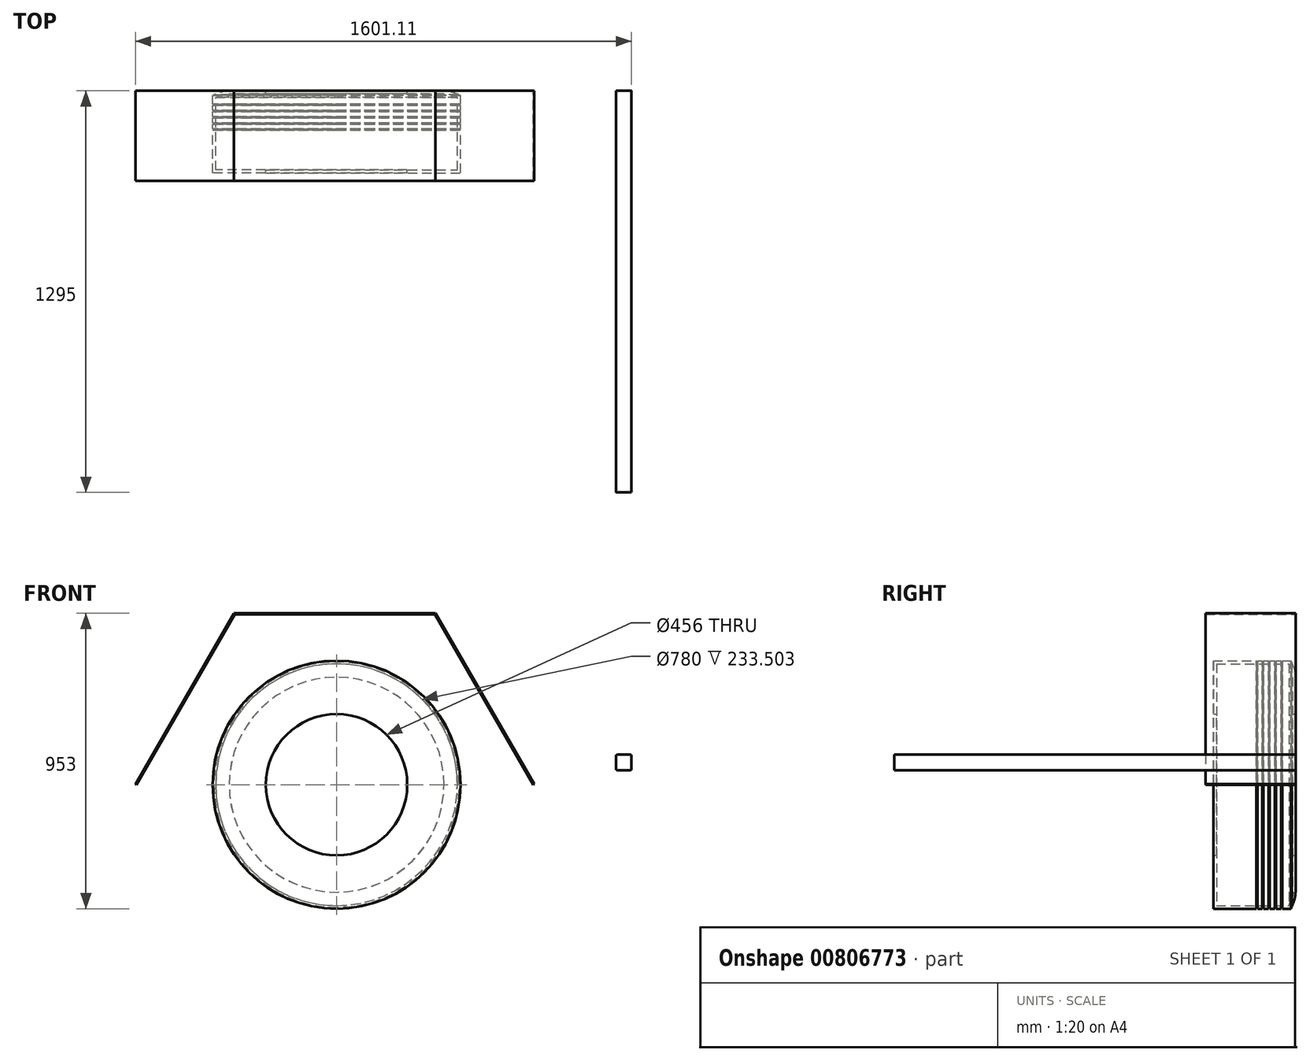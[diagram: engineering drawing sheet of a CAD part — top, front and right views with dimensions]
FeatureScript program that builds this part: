
annotation { "Feature Type Name" : "Feature", "Feature Type Description" : "" }
export const myFeature = defineFeature(function(context is Context, id is Id, definition is map)
    precondition{}
    {
        {
            var Q0;
            Q0=qCreatedBy(makeId("Front.planeOp"),FACE);
            var sketch = newSketch(context, id + "F0", { "sketchPlane" : qUnion([Q0])});
            skCircle(sketch, "E0", {"center": v(0, 0) * mm, "radius": 400 * mm});
            skCircle(sketch, "E1.0", {"center": v(0, 0) * mm, "radius": 228 * mm});
            skSolve(sketch);
        }
        {
            var Q0;
            Q0=makeQuery(id+"F0.imprint","IMPRINT",FACE,{"disambiguationData":[TD([[makeQuery(id+"F0.imprint","IMPRINT",EDGE,{"derivedFrom":sQuery(id+"F0.wireOp",EDGE,"E0")}),1.0]])]});
            extrude(context, id + "F1", {"entities" : qUnion([Q0]), "depth" : 265 * mm, "offsetDistance" : 25 * mm});
        }
        {
            var Q0;
            Q0=qCreatedBy(makeId("Right.planeOp"),FACE);
            var sketch = newSketch(context, id + "F2", { "sketchPlane" : qUnion([Q0])});
            skLineSegment(sketch, "E2", {"start": v(-265, 400) * mm, "end": v(0, 400) * mm});
            skLineSegment(sketch, "E3.0", {"start": v(-265, -400) * mm, "end": v(-265, 400) * mm});
            skLineSegment(sketch, "E4", {"start": v(0, 228) * mm, "end": v(-265, 228) * mm});
            skLineSegment(sketch, "E5", {"start": v(-15, 400) * mm, "end": v(-15, 228) * mm, "construction": true});
            skLineSegment(sketch, "E6", {"start": v(-25, 400) * mm, "end": v(-25, 228) * mm, "construction": true});
            skFitSpline(sketch, "E7", {"points": [v(-15, 400) * mm, v(0, 346.7) * mm, v(-25, 228) * mm], "startDerivative": vector(53.15, -118.74) * mm, "endDerivative": vector(-65.5, -218.8) * mm});
            skArc(sketch, "E8", {"start": v(-12.04, 393.34) * mm, "mid": v(-16.38, 398.48) * mm, "end": v(-22.93, 400) * mm});
            skPoint(sketch, "E8.first.point", {"position": v(-12.33, 393.99) * mm});
            skPoint(sketch, "E8.second.point", {"position": v(-16.14, 398.33) * mm});
            skPoint(sketch, "E8.third.point", {"position": v(-22.93, 400) * mm});
            skLineSegment(sketch, "E9", {"start": v(-132.5, 400) * mm, "end": v(-132.5, -399.15) * mm, "construction": true});
            skArc(sketch, "E10.MirrorCS", {"start": v(-252.96, 393.34) * mm, "mid": v(-248.62, 398.48) * mm, "end": v(-242.07, 400) * mm});
            skFitSpline(sketch, "E11.MirrorCS", {"points": [v(-250, 400) * mm, v(-265, 346.7) * mm, v(-240, 228) * mm], "startDerivative": vector(-53.15, -118.74) * mm, "endDerivative": vector(65.5, -218.8) * mm});
            skLineSegment(sketch, "E12", {"start": v(-22.93, 400) * mm, "end": v(0, 400) * mm});
            skLineSegment(sketch, "E13", {"start": v(0, 400) * mm, "end": v(0, 228) * mm});
            skLineSegment(sketch, "E14", {"start": v(0, 228) * mm, "end": v(-25, 228) * mm});
            skLineSegment(sketch, "E15", {"start": v(-242.07, 400) * mm, "end": v(-265, 400) * mm});
            skLineSegment(sketch, "E16", {"start": v(-265, 400) * mm, "end": v(-265, 228) * mm});
            skLineSegment(sketch, "E17", {"start": v(-265, 228) * mm, "end": v(-240, 228) * mm});
            skLineSegment(sketch, "E18.bottom", {"start": v(-138.22, 400) * mm, "end": v(-141.84, 400) * mm});
            skLineSegment(sketch, "E18.top", {"start": v(-138.22, 395.6) * mm, "end": v(-141.84, 395.6) * mm});
            skLineSegment(sketch, "E18.left", {"start": v(-138.22, 400) * mm, "end": v(-138.22, 395.6) * mm});
            skLineSegment(sketch, "E18.right", {"start": v(-141.84, 400) * mm, "end": v(-141.84, 395.6) * mm});
            skLineSegment(sketch, "E19.1.0.0", {"start": v(-158.22, 400) * mm, "end": v(-161.84, 400) * mm});
            skLineSegment(sketch, "E19.1.0.1", {"start": v(-158.22, 400) * mm, "end": v(-158.22, 395.6) * mm});
            skLineSegment(sketch, "E19.1.0.2", {"start": v(-161.84, 400) * mm, "end": v(-161.84, 395.6) * mm});
            skLineSegment(sketch, "E19.1.0.3", {"start": v(-158.22, 395.6) * mm, "end": v(-161.84, 395.6) * mm});
            skLineSegment(sketch, "E19.2.0.0", {"start": v(-178.22, 400) * mm, "end": v(-181.84, 400) * mm});
            skLineSegment(sketch, "E19.2.0.1", {"start": v(-178.22, 400) * mm, "end": v(-178.22, 395.6) * mm});
            skLineSegment(sketch, "E19.2.0.2", {"start": v(-181.84, 400) * mm, "end": v(-181.84, 395.6) * mm});
            skLineSegment(sketch, "E19.2.0.3", {"start": v(-178.22, 395.6) * mm, "end": v(-181.84, 395.6) * mm});
            skLineSegment(sketch, "E19.3.0.0", {"start": v(-198.22, 400) * mm, "end": v(-201.84, 400) * mm});
            skLineSegment(sketch, "E19.3.0.1", {"start": v(-198.22, 400) * mm, "end": v(-198.22, 395.6) * mm});
            skLineSegment(sketch, "E19.3.0.2", {"start": v(-201.84, 400) * mm, "end": v(-201.84, 395.6) * mm});
            skLineSegment(sketch, "E19.3.0.3", {"start": v(-198.22, 395.6) * mm, "end": v(-201.84, 395.6) * mm});
            skLineSegment(sketch, "E19.4.0.0", {"start": v(-218.22, 400) * mm, "end": v(-221.84, 400) * mm});
            skLineSegment(sketch, "E19.4.0.1", {"start": v(-218.22, 400) * mm, "end": v(-218.22, 395.6) * mm});
            skLineSegment(sketch, "E19.4.0.2", {"start": v(-221.84, 400) * mm, "end": v(-221.84, 395.6) * mm});
            skLineSegment(sketch, "E19.4.0.3", {"start": v(-218.22, 395.6) * mm, "end": v(-221.84, 395.6) * mm});
            skLineSegment(sketch, "E19.5.0.0", {"start": v(-238.22, 400) * mm, "end": v(-241.84, 400) * mm});
            skLineSegment(sketch, "E19.5.0.1", {"start": v(-238.22, 400) * mm, "end": v(-238.22, 395.6) * mm});
            skLineSegment(sketch, "E19.5.0.2", {"start": v(-241.84, 400) * mm, "end": v(-241.84, 395.6) * mm});
            skLineSegment(sketch, "E19.5.0.3", {"start": v(-238.22, 395.6) * mm, "end": v(-241.84, 395.6) * mm});
            skLineSegment(sketch, "E19.direction1", {"start": v(-141.84, 400) * mm, "end": v(-161.84, 400) * mm, "construction": true});
            skLineSegment(sketch, "E20.MirrorCS", {"start": v(-26.78, 400) * mm, "end": v(-23.16, 400) * mm});
            skLineSegment(sketch, "E21.MirrorCS", {"start": v(-23.16, 400) * mm, "end": v(-23.16, 395.6) * mm});
            skLineSegment(sketch, "E22.MirrorCS", {"start": v(-26.78, 395.6) * mm, "end": v(-23.16, 395.6) * mm});
            skLineSegment(sketch, "E23.MirrorCS", {"start": v(-26.78, 400) * mm, "end": v(-26.78, 395.6) * mm});
            skLineSegment(sketch, "E24.MirrorCS", {"start": v(-43.16, 400) * mm, "end": v(-43.16, 395.6) * mm});
            skLineSegment(sketch, "E25.MirrorCS", {"start": v(-46.78, 395.6) * mm, "end": v(-43.16, 395.6) * mm});
            skLineSegment(sketch, "E26.MirrorCS", {"start": v(-46.78, 400) * mm, "end": v(-46.78, 395.6) * mm});
            skLineSegment(sketch, "E27.MirrorCS", {"start": v(-46.78, 400) * mm, "end": v(-43.16, 400) * mm});
            skLineSegment(sketch, "E28.MirrorCS", {"start": v(-63.16, 400) * mm, "end": v(-63.16, 395.6) * mm});
            skLineSegment(sketch, "E29.MirrorCS", {"start": v(-66.78, 395.6) * mm, "end": v(-63.16, 395.6) * mm});
            skLineSegment(sketch, "E30.MirrorCS", {"start": v(-66.78, 400) * mm, "end": v(-66.78, 395.6) * mm});
            skLineSegment(sketch, "E31.MirrorCS", {"start": v(-66.78, 400) * mm, "end": v(-63.16, 400) * mm});
            skLineSegment(sketch, "E32.MirrorCS", {"start": v(-83.16, 400) * mm, "end": v(-83.16, 395.6) * mm});
            skLineSegment(sketch, "E33.MirrorCS", {"start": v(-86.78, 395.6) * mm, "end": v(-83.16, 395.6) * mm});
            skLineSegment(sketch, "E34.MirrorCS", {"start": v(-86.78, 400) * mm, "end": v(-86.78, 395.6) * mm});
            skLineSegment(sketch, "E35.MirrorCS", {"start": v(-86.78, 400) * mm, "end": v(-83.16, 400) * mm});
            skLineSegment(sketch, "E36.MirrorCS", {"start": v(-103.16, 400) * mm, "end": v(-103.16, 395.6) * mm});
            skLineSegment(sketch, "E37.MirrorCS", {"start": v(-106.78, 395.6) * mm, "end": v(-103.16, 395.6) * mm});
            skLineSegment(sketch, "E38.MirrorCS", {"start": v(-106.78, 400) * mm, "end": v(-106.78, 395.6) * mm});
            skLineSegment(sketch, "E39.MirrorCS", {"start": v(-106.78, 400) * mm, "end": v(-103.16, 400) * mm});
            skLineSegment(sketch, "E40.MirrorCS", {"start": v(-123.16, 400) * mm, "end": v(-123.16, 395.6) * mm});
            skLineSegment(sketch, "E41.MirrorCS", {"start": v(-126.78, 395.6) * mm, "end": v(-123.16, 395.6) * mm});
            skLineSegment(sketch, "E42.MirrorCS", {"start": v(-126.78, 400) * mm, "end": v(-126.78, 395.6) * mm});
            skLineSegment(sketch, "E43.MirrorCS", {"start": v(-126.78, 400) * mm, "end": v(-123.16, 400) * mm});
            skSolve(sketch);
        }
        {
            var Q0;
            Q0=qCreatedBy(makeId("Right.planeOp"),FACE);
            var sketch = newSketch(context, id + "F3", { "sketchPlane" : qUnion([Q0])});
            skLineSegment(sketch, "E44", {"start": v(0, 0) * mm, "end": v(-286.12, 0) * mm, "construction": true});
            skSolve(sketch);
        }
        {
            var Q0;
            {var subQ0=sQuery(id+"F2.wireOp",EDGE,"E17");Q0=makeQuery(id+"F2.imprint","IMPRINT",FACE,{"disambiguationData":[TD([[makeQuery(id+"F2.imprint","IMPRINT",EDGE,{"derivedFrom":subQ0}),1.0]])]});}
            var Q1;
            {var subQ3=sQuery(id+"F2.wireOp",EDGE,"E10.MirrorCS");var subQ5=sQuery(id+"F2.wireOp",EDGE,"E11.MirrorCS");var subQ6=makeQuery(id+"F2.imprint","INTERSECT",VERTEX,{"disambiguationData":[OD(0.0)],"derivedFrom":[subQ3,subQ5]});Q1=makeQuery(id+"F2.imprint","IMPRINT",FACE,{"disambiguationData":[TD([[makeQuery(id+"F2.imprint","IMPRINT",EDGE,{"disambiguationData":[TD([[subQ6,-1.0]])],"derivedFrom":subQ3}),1.0]])]});}
            var Q2;
            {var subQ3=sQuery(id+"F2.wireOp",EDGE,"E8");var subQ5=sQuery(id+"F2.wireOp",EDGE,"E7");var subQ7=makeQuery(id+"F2.imprint","INTERSECT",VERTEX,{"disambiguationData":[OD(1.0)],"derivedFrom":[subQ5,subQ3]});Q2=makeQuery(id+"F2.imprint","IMPRINT",FACE,{"disambiguationData":[TD([[makeQuery(id+"F2.imprint","IMPRINT",EDGE,{"disambiguationData":[TD([[subQ7,-1.0]])],"derivedFrom":subQ5}),1.0]])]});}
            var Q3;
            {var subQ0=sQuery(id+"F2.wireOp",EDGE,"E14");Q3=makeQuery(id+"F2.imprint","IMPRINT",FACE,{"disambiguationData":[TD([[makeQuery(id+"F2.imprint","IMPRINT",EDGE,{"derivedFrom":subQ0}),-1.0]])]});}
            var Q4;
            Q4=sQuery(id+"F3.wireOp",EDGE,"E44");
            var Q5;
            Q5=sQuery(id+"F3.wireOp",EDGE,"E44");
            revolve(context, id + "F4", {"surfaceOperationType" : NewSurfaceOperationType.NEW, "entities" : qUnion([Q0, Q1, Q2, Q3]), "surfaceEntities" : qUnion([Q4]), "axis" : qUnion([Q5]), "revolveType" : RevolveType.FULL});
        }
        {
            var Q0;
            Q0=makeQuery(id+"F4.opRevolve","SWEPT_BODY",BODY,{"disambiguationData":[OSD([sQuery(id+"F2.wireOp",EDGE,"E10.MirrorCS"),sQuery(id+"F2.wireOp",EDGE,"E11.MirrorCS"),sQuery(id+"F2.wireOp",EDGE,"E15"),sQuery(id+"F2.wireOp",EDGE,"E16")])]});
            var Q1;
            Q1=makeQuery(id+"F4.opRevolve","SWEPT_BODY",BODY,{"disambiguationData":[OSD([sQuery(id+"F2.wireOp",EDGE,"E11.MirrorCS"),sQuery(id+"F2.wireOp",EDGE,"E16"),sQuery(id+"F2.wireOp",EDGE,"E17")])]});
            var Q2;
            Q2=makeQuery(id+"F4.opRevolve","SWEPT_BODY",BODY,{"disambiguationData":[OSD([sQuery(id+"F2.wireOp",EDGE,"E7"),sQuery(id+"F2.wireOp",EDGE,"E8"),sQuery(id+"F2.wireOp",EDGE,"E12"),sQuery(id+"F2.wireOp",EDGE,"E13")])]});
            var Q3;
            Q3=makeQuery(id+"F4.opRevolve","SWEPT_BODY",BODY,{"disambiguationData":[OSD([sQuery(id+"F2.wireOp",EDGE,"E7"),sQuery(id+"F2.wireOp",EDGE,"E13"),sQuery(id+"F2.wireOp",EDGE,"E14")])]});
            var Q4;
            Q4=makeQuery(id+"F1.opExtrude","SWEPT_BODY",BODY,{"disambiguationData":[OSD([sQuery(id+"F0.wireOp",EDGE,"E0"),sQuery(id+"F0.wireOp",EDGE,"E1.0")])]});
            booleanBodies(context, id + "F5", {"operationType" : BooleanOperationType.SUBTRACTION, "tools" : qUnion([Q0, Q1, Q2, Q3]), "targets" : qUnion([Q4])});
        }
        {
            var Q0;
            Q0=makeQuery(id+"F1.opExtrude","SWEPT_FACE",FACE,{"disambiguationData":[OSD([sQuery(id+"F0.wireOp",EDGE,"E1.0")])]});
            shell(context, id + "F6", {"entities" : qUnion([Q0]), "thickness" : 10 * mm});
        }
        {
            var Q0;
            Q0=makeQuery(id+"F2.imprint","IMPRINT",FACE,{"disambiguationData":[TD([[makeQuery(id+"F2.imprint","IMPRINT",EDGE,{"derivedFrom":sQuery(id+"F2.wireOp",EDGE,"E19.5.0.0")}),1.0]])]});
            var Q1;
            Q1=makeQuery(id+"F2.imprint","IMPRINT",FACE,{"disambiguationData":[TD([[makeQuery(id+"F2.imprint","IMPRINT",EDGE,{"derivedFrom":sQuery(id+"F2.wireOp",EDGE,"E19.4.0.0")}),1.0]])]});
            var Q2;
            Q2=makeQuery(id+"F2.imprint","IMPRINT",FACE,{"disambiguationData":[TD([[makeQuery(id+"F2.imprint","IMPRINT",EDGE,{"derivedFrom":sQuery(id+"F2.wireOp",EDGE,"E19.3.0.0")}),1.0]])]});
            var Q3;
            Q3=makeQuery(id+"F2.imprint","IMPRINT",FACE,{"disambiguationData":[TD([[makeQuery(id+"F2.imprint","IMPRINT",EDGE,{"derivedFrom":sQuery(id+"F2.wireOp",EDGE,"E19.2.0.0")}),1.0]])]});
            var Q4;
            Q4=makeQuery(id+"F2.imprint","IMPRINT",FACE,{"disambiguationData":[TD([[makeQuery(id+"F2.imprint","IMPRINT",EDGE,{"derivedFrom":sQuery(id+"F2.wireOp",EDGE,"E19.1.0.0")}),1.0]])]});
            var Q5;
            Q5=makeQuery(id+"F2.imprint","IMPRINT",FACE,{"disambiguationData":[TD([[makeQuery(id+"F2.imprint","IMPRINT",EDGE,{"derivedFrom":sQuery(id+"F2.wireOp",EDGE,"E18.bottom")}),1.0]])]});
            var Q6;
            Q6=makeQuery(id+"F2.imprint","IMPRINT",FACE,{"disambiguationData":[TD([[makeQuery(id+"F2.imprint","IMPRINT",EDGE,{"derivedFrom":sQuery(id+"F2.wireOp",EDGE,"E40.MirrorCS")}),-1.0]])]});
            var Q7;
            Q7=makeQuery(id+"F2.imprint","IMPRINT",FACE,{"disambiguationData":[TD([[makeQuery(id+"F2.imprint","IMPRINT",EDGE,{"derivedFrom":sQuery(id+"F2.wireOp",EDGE,"E36.MirrorCS")}),-1.0]])]});
            var Q8;
            Q8=makeQuery(id+"F2.imprint","IMPRINT",FACE,{"disambiguationData":[TD([[makeQuery(id+"F2.imprint","IMPRINT",EDGE,{"derivedFrom":sQuery(id+"F2.wireOp",EDGE,"E32.MirrorCS")}),-1.0]])]});
            var Q9;
            Q9=makeQuery(id+"F2.imprint","IMPRINT",FACE,{"disambiguationData":[TD([[makeQuery(id+"F2.imprint","IMPRINT",EDGE,{"derivedFrom":sQuery(id+"F2.wireOp",EDGE,"E28.MirrorCS")}),-1.0]])]});
            var Q10;
            Q10=makeQuery(id+"F2.imprint","IMPRINT",FACE,{"disambiguationData":[TD([[makeQuery(id+"F2.imprint","IMPRINT",EDGE,{"derivedFrom":sQuery(id+"F2.wireOp",EDGE,"E24.MirrorCS")}),-1.0]])]});
            var Q11;
            Q11=makeQuery(id+"F2.imprint","IMPRINT",FACE,{"disambiguationData":[TD([[makeQuery(id+"F2.imprint","IMPRINT",EDGE,{"derivedFrom":sQuery(id+"F2.wireOp",EDGE,"E20.MirrorCS")}),-1.0]])]});
            var Q12;
            Q12=sQuery(id+"F3.wireOp",EDGE,"E44");
            revolve(context, id + "F7", {"operationType" : NewBodyOperationType.REMOVE, "surfaceOperationType" : NewSurfaceOperationType.NEW, "entities" : qUnion([Q0, Q1, Q2, Q3, Q4, Q5, Q6, Q7, Q8, Q9, Q10, Q11]), "axis" : qUnion([Q12]), "revolveType" : RevolveType.FULL});
        }
        {
            var Q0;
            Q0=qCreatedBy(makeId("Front.planeOp"),FACE);
            var sketch = newSketch(context, id + "F8", { "sketchPlane" : qUnion([Q0])});
            skLineSegment(sketch, "E45.bottom", {"start": v(901.88, 96.72) * mm, "end": v(951.88, 96.72) * mm});
            skLineSegment(sketch, "E45.top", {"start": v(901.88, 46.72) * mm, "end": v(951.88, 46.72) * mm});
            skLineSegment(sketch, "E45.left", {"start": v(901.88, 96.72) * mm, "end": v(901.88, 46.72) * mm});
            skLineSegment(sketch, "E45.right", {"start": v(951.88, 96.72) * mm, "end": v(951.88, 46.72) * mm});
            skSolve(sketch);
        }
        {
            var Q0;
            Q0=makeQuery(id+"F8.imprint","IMPRINT",FACE,{"disambiguationData":[TD([[makeQuery(id+"F8.imprint","IMPRINT",EDGE,{"derivedFrom":sQuery(id+"F8.wireOp",EDGE,"E45.bottom")}),-1.0]])]});
            extrude(context, id + "F9", {"entities" : qUnion([Q0]), "depth" : 1295 * mm, "offsetDistance" : 25 * mm});
        }
        {
            var Q0;
            Q0=makeQuery(id+"F9.opExtrude","SWEPT_EDGE",EDGE,{"disambiguationData":[OSD([sQuery(id+"F8.wireOp",EDGE,"E45.bottom"),sQuery(id+"F8.wireOp",EDGE,"E45.right")])]});
            var Q1;
            Q1=makeQuery(id+"F9.opExtrude","SWEPT_EDGE",EDGE,{"disambiguationData":[OSD([sQuery(id+"F8.wireOp",EDGE,"E45.top"),sQuery(id+"F8.wireOp",EDGE,"E45.right")])]});
            var Q2;
            Q2=makeQuery(id+"F9.opExtrude","SWEPT_EDGE",EDGE,{"disambiguationData":[OSD([sQuery(id+"F8.wireOp",EDGE,"E45.bottom"),sQuery(id+"F8.wireOp",EDGE,"E45.left")])]});
            var Q3;
            Q3=makeQuery(id+"F9.opExtrude","SWEPT_EDGE",EDGE,{"disambiguationData":[OSD([sQuery(id+"F8.wireOp",EDGE,"E45.top"),sQuery(id+"F8.wireOp",EDGE,"E45.left")])]});
            fillet(context, id + "F10", {"entities" : qUnion([Q0, Q1, Q2, Q3]), "radius" : 4 * mm, "tangentPropagation" : true, "allowEdgeOverflow" : false});
        }
        {
            var Q0;
            Q0=qCreatedBy(makeId("Front.planeOp"),FACE);
            var sketch = newSketch(context, id + "F11", { "sketchPlane" : qUnion([Q0])});
            skCircle(sketch, "E46.0", {"center": v(0, 0) * mm, "radius": 400 * mm});
            skLineSegment(sketch, "E47", {"start": v(317.54, 550) * mm, "end": v(-329.09, 550) * mm});
            skLineSegment(sketch, "E48", {"start": v(-329.09, 550) * mm, "end": v(-646.63, 0) * mm});
            skLineSegment(sketch, "E49", {"start": v(317.54, 550) * mm, "end": v(635.09, 0) * mm});
            skLineSegment(sketch, "E50.0", {"start": v(319.27, 553) * mm, "end": v(637.68, 1.5) * mm});
            skLineSegment(sketch, "E51.0", {"start": v(319.27, 553) * mm, "end": v(-330.82, 553) * mm});
            skLineSegment(sketch, "E52.0", {"start": v(-330.82, 553) * mm, "end": v(-649.23, 1.5) * mm});
            skLineSegment(sketch, "E53", {"start": v(637.68, 1.5) * mm, "end": v(635.09, 0) * mm});
            skLineSegment(sketch, "E54", {"start": v(-646.63, 0) * mm, "end": v(-649.23, 1.5) * mm});
            skSolve(sketch);
        }
        {
            var Q0;
            Q0=makeQuery(id+"F11.imprint","IMPRINT",FACE,{"disambiguationData":[TD([[makeQuery(id+"F11.imprint","IMPRINT",EDGE,{"derivedFrom":sQuery(id+"F11.wireOp",EDGE,"E47")}),-1.0]])]});
            extrude(context, id + "F12", {"entities" : qUnion([Q0]), "depth" : 290 * mm, "offsetDistance" : 25 * mm});
        }
    });
